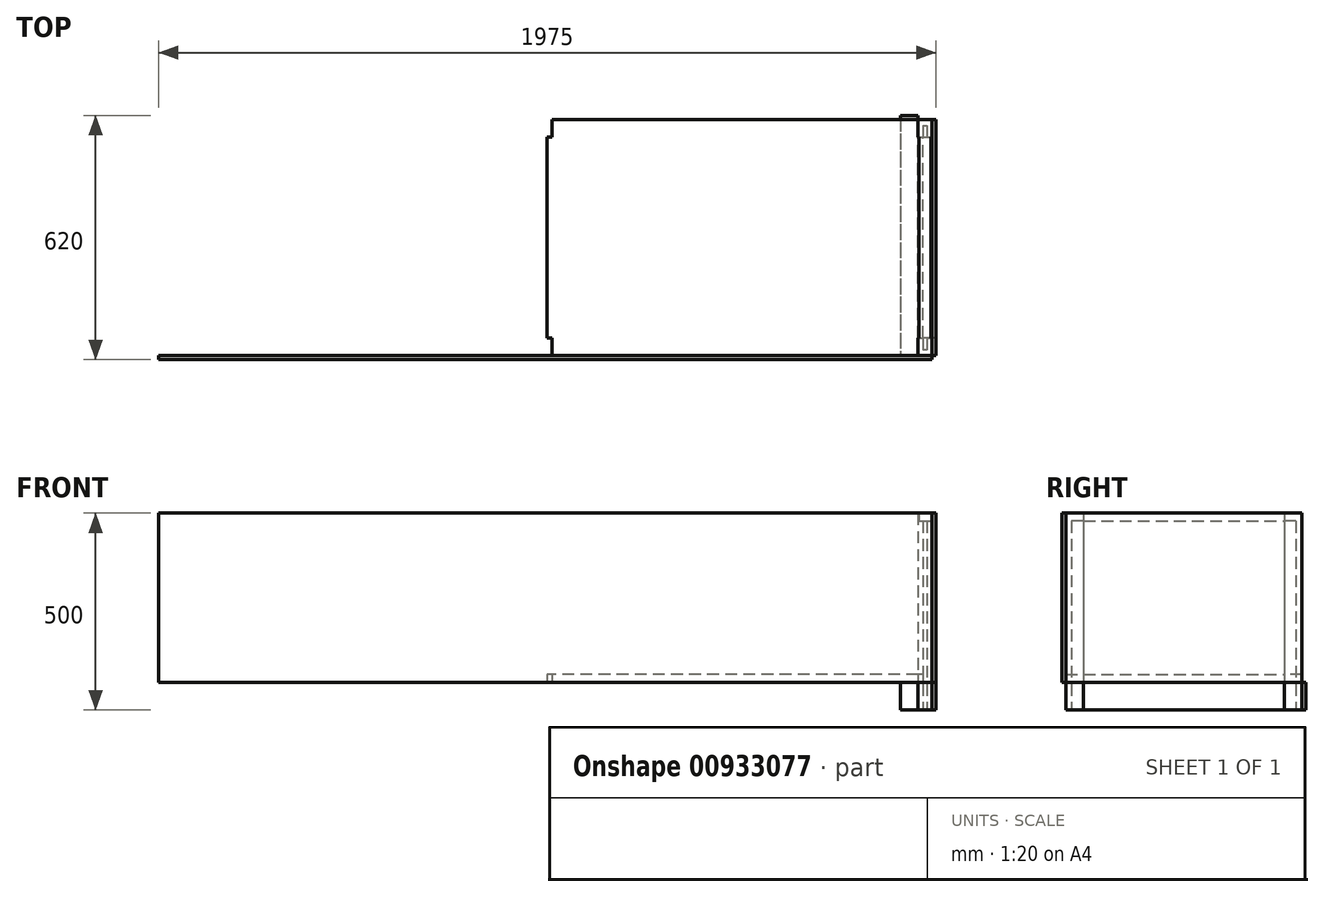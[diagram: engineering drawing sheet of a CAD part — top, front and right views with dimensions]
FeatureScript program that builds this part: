
annotation { "Feature Type Name" : "Feature", "Feature Type Description" : "" }
export const myFeature = defineFeature(function(context is Context, id is Id, definition is map)
    precondition{}
    {
        {
            var Q0;
            Q0=qCreatedBy(makeId("Top.planeOp"),FACE);
            var sketch = newSketch(context, id + "F0", { "sketchPlane" : qUnion([Q0])});
            skLineSegment(sketch, "E0.bottom", {"start": v(-17.5, 300) * mm, "end": v(17.5, 300) * mm});
            skLineSegment(sketch, "E0.top", {"start": v(-17.5, 255) * mm, "end": v(-5, 255) * mm});
            skLineSegment(sketch, "E0.left", {"start": v(-17.5, 300) * mm, "end": v(-17.5, 255) * mm});
            skLineSegment(sketch, "E0.right", {"start": v(17.5, 300) * mm, "end": v(17.5, 255) * mm});
            skLineSegment(sketch, "E1.bottom", {"start": v(-5, 285) * mm, "end": v(5, 285) * mm});
            skLineSegment(sketch, "E1.left", {"start": v(-5, 285) * mm, "end": v(-5, 255) * mm});
            skLineSegment(sketch, "E1.right", {"start": v(5, 285) * mm, "end": v(5, 255) * mm});
            skLineSegment(sketch, "E2.trimOffspring", {"start": v(5, 255) * mm, "end": v(17.5, 255) * mm});
            skLineSegment(sketch, "E3.bottom", {"start": v(-17.5, -255) * mm, "end": v(-5, -255) * mm});
            skLineSegment(sketch, "E3.top", {"start": v(-17.5, -300) * mm, "end": v(17.5, -300) * mm});
            skLineSegment(sketch, "E3.left", {"start": v(-17.5, -255) * mm, "end": v(-17.5, -300) * mm});
            skLineSegment(sketch, "E3.right", {"start": v(17.5, -255) * mm, "end": v(17.5, -300) * mm});
            skLineSegment(sketch, "E4.top", {"start": v(-5, -285) * mm, "end": v(5, -285) * mm});
            skLineSegment(sketch, "E4.left", {"start": v(-5, -255) * mm, "end": v(-5, -285) * mm});
            skLineSegment(sketch, "E4.right", {"start": v(5, -255) * mm, "end": v(5, -285) * mm});
            skLineSegment(sketch, "E5.trimOffspring", {"start": v(5, -255) * mm, "end": v(17.5, -255) * mm});
            skSolve(sketch);
        }
        {
            var Q0;
            Q0=qSketchRegion(id+"F0",true);
            extrude(context, id + "F1", {"entities" : qUnion([Q0]), "depth" : 500 * mm, "offsetDistance" : 25 * mm});
        }
        {
            var Q0;
            Q0=makeQuery(id+"F1.opExtrude","SWEPT_FACE",FACE,{"disambiguationData":[OSD([sQuery(id+"F0.wireOp",EDGE,"E1.bottom")])]});
            var sketch = newSketch(context, id + "F2", { "sketchPlane" : qUnion([Q0])});
            skLineSegment(sketch, "E6.bottom", {"start": v(-15, 500) * mm, "end": v(15, 500) * mm});
            skLineSegment(sketch, "E6.top", {"start": v(-15, 480) * mm, "end": v(15, 480) * mm});
            skLineSegment(sketch, "E6.left", {"start": v(-15, 500) * mm, "end": v(-15, 480) * mm});
            skLineSegment(sketch, "E6.right", {"start": v(15, 500) * mm, "end": v(15, 480) * mm});
            skSolve(sketch);
        }
        {
            var Q0;
            Q0=qSketchRegion(id+"F2",true);
            var Q1;
            Q1=makeQuery(id+"F1.opExtrude","SWEPT_FACE",FACE,{"disambiguationData":[OSD([sQuery(id+"F0.wireOp",EDGE,"E4.top")])]});
            extrude(context, id + "F3", {"entities" : qUnion([Q0]), "operationType" : NewBodyOperationType.ADD, "endBound" : BoundingType.UP_TO_SURFACE, "depth" : 25 * mm, "endBoundEntityFace" : qUnion([Q1]), "offsetDistance" : 25 * mm});
        }
        {
            var Q0;
            Q0=makeQuery(id+"F1.opExtrude","SWEPT_FACE",FACE,{"disambiguationData":[OSD([sQuery(id+"F0.wireOp",EDGE,"E3.top")])]});
            var sketch = newSketch(context, id + "F4", { "sketchPlane" : qUnion([Q0])});
            skLineSegment(sketch, "E7.bottom", {"start": v(-62.5, 70) * mm, "end": v(-17.5, 70) * mm});
            skLineSegment(sketch, "E7.top", {"start": v(-62.5, 0) * mm, "end": v(-17.5, 0) * mm});
            skLineSegment(sketch, "E7.left", {"start": v(-62.5, 70) * mm, "end": v(-62.5, 0) * mm});
            skLineSegment(sketch, "E7.right", {"start": v(-17.5, 70) * mm, "end": v(-17.5, 0) * mm});
            skSolve(sketch);
        }
        {
            var Q0;
            Q0=qSketchRegion(id+"F4",true);
            extrude(context, id + "F5", {"entities" : qUnion([Q0]), "oppositeDirection" : true, "depth" : 610 * mm, "offsetDistance" : 25 * mm});
        }
        {
            var Q0;
            Q0=makeQuery(id+"F1.opExtrude","SWEPT_FACE",FACE,{"disambiguationData":[OSD([sQuery(id+"F0.wireOp",EDGE,"E3.top")])]});
            var sketch = newSketch(context, id + "F6", { "sketchPlane" : qUnion([Q0])});
            skLineSegment(sketch, "E8.bottom", {"start": v(-1947.5, 500) * mm, "end": v(17.5, 500) * mm});
            skLineSegment(sketch, "E8.top", {"start": v(-1947.5, 70) * mm, "end": v(17.5, 70) * mm});
            skLineSegment(sketch, "E8.left", {"start": v(-1947.5, 500) * mm, "end": v(-1947.5, 70) * mm});
            skLineSegment(sketch, "E8.right", {"start": v(17.5, 500) * mm, "end": v(17.5, 70) * mm});
            skSolve(sketch);
        }
        {
            var Q0;
            Q0=qSketchRegion(id+"F6",true);
            extrude(context, id + "F7", {"entities" : qUnion([Q0]), "depth" : 10 * mm, "offsetDistance" : 25 * mm});
        }
        {
            var Q0;
            Q0=makeQuery(id+"F1.opExtrude","SWEPT_FACE",FACE,{"disambiguationData":[OSD([sQuery(id+"F0.wireOp",EDGE,"E3.right")])]});
            var sketch = newSketch(context, id + "F8", { "sketchPlane" : qUnion([Q0])});
            skLineSegment(sketch, "E9.bottom", {"start": v(-300, 500) * mm, "end": v(300, 500) * mm});
            skLineSegment(sketch, "E9.top", {"start": v(-300, 70) * mm, "end": v(300, 70) * mm});
            skLineSegment(sketch, "E9.left", {"start": v(-300, 500) * mm, "end": v(-300, 70) * mm});
            skLineSegment(sketch, "E9.right", {"start": v(300, 500) * mm, "end": v(300, 70) * mm});
            skSolve(sketch);
        }
        {
            var Q0;
            Q0=qSketchRegion(id+"F8",true);
            extrude(context, id + "F9", {"entities" : qUnion([Q0]), "depth" : 10 * mm, "offsetDistance" : 25 * mm});
        }
        {
            var Q0;
            Q0=makeQuery(id+"F5.opExtrude","SWEPT_FACE",FACE,{"disambiguationData":[OSD([sQuery(id+"F4.wireOp",EDGE,"E7.bottom")])]});
            var sketch = newSketch(context, id + "F10", { "sketchPlane" : qUnion([Q0])});
            skLineSegment(sketch, "E10.bottom", {"start": v(-5, -255) * mm, "end": v(-17.5, -255) * mm});
            skLineSegment(sketch, "E10.top", {"start": v(-5, 255) * mm, "end": v(-17.5, 255) * mm});
            skLineSegment(sketch, "E10.left", {"start": v(-5, -255) * mm, "end": v(-5, 255) * mm});
            skLineSegment(sketch, "E10.right", {"start": v(-960, -255) * mm, "end": v(-960, 255) * mm});
            skLineSegment(sketch, "E11.bottom", {"start": v(-17.5, -300) * mm, "end": v(-947.5, -300) * mm});
            skLineSegment(sketch, "E11.top", {"start": v(-17.5, 300) * mm, "end": v(-947.5, 300) * mm});
            skLineSegment(sketch, "E11.left", {"start": v(-17.5, -300) * mm, "end": v(-17.5, -255) * mm});
            skLineSegment(sketch, "E11.right", {"start": v(-947.5, -300) * mm, "end": v(-947.5, -255) * mm});
            skLineSegment(sketch, "E12", {"start": v(-482.5, 300) * mm, "end": v(-482.5, -300) * mm, "construction": true});
            skLineSegment(sketch, "E13", {"start": v(-5, 0) * mm, "end": v(-960, 0) * mm, "construction": true});
            skLineSegment(sketch, "E14.trimOffspring", {"start": v(-947.5, -255) * mm, "end": v(-960, -255) * mm});
            skLineSegment(sketch, "E15.trimOffspring", {"start": v(-947.5, 255) * mm, "end": v(-947.5, 300) * mm});
            skLineSegment(sketch, "E16.trimOffspring", {"start": v(-947.5, 255) * mm, "end": v(-960, 255) * mm});
            skLineSegment(sketch, "E17.trimOffspring", {"start": v(-17.5, 255) * mm, "end": v(-17.5, 300) * mm});
            skSolve(sketch);
        }
        {
            var Q0;
            Q0=qSketchRegion(id+"F10",true);
            extrude(context, id + "F11", {"entities" : qUnion([Q0]), "depth" : 20 * mm, "offsetDistance" : 25 * mm});
        }
        {
            var Q0;
            Q0=makeQuery(id+"F1.opExtrude","SWEPT_FACE",FACE,{"disambiguationData":[OSD([sQuery(id+"F0.wireOp",EDGE,"E2.trimOffspring")])]});
            var sketch = newSketch(context, id + "F12", { "sketchPlane" : qUnion([Q0])});
            skLineSegment(sketch, "E18.bottom", {"start": v(-17.5, 70) * mm, "end": v(27.5, 70) * mm});
            skLineSegment(sketch, "E18.top", {"start": v(-17.5, 0) * mm, "end": v(27.5, 0) * mm});
            skLineSegment(sketch, "E18.left", {"start": v(-17.5, 70) * mm, "end": v(-17.5, 0) * mm});
            skLineSegment(sketch, "E18.right", {"start": v(27.5, 70) * mm, "end": v(27.5, 0) * mm});
            skSolve(sketch);
        }
        {
            var Q0;
            Q0 = qSketchRegion(id + "F12", true);
            var Q1;
            Q1=makeQuery(id+"F1.opExtrude","SWEPT_FACE",FACE,{"disambiguationData":[OSD([sQuery(id+"F0.wireOp",EDGE,"E5.trimOffspring")])]});
            extrude(context, id + "F13", {"entities" : qUnion([Q0]), "endBound" : BoundingType.UP_TO_SURFACE, "depth" : 25 * mm, "endBoundEntityFace" : qUnion([Q1]), "offsetDistance" : 25 * mm});
        }
    });
